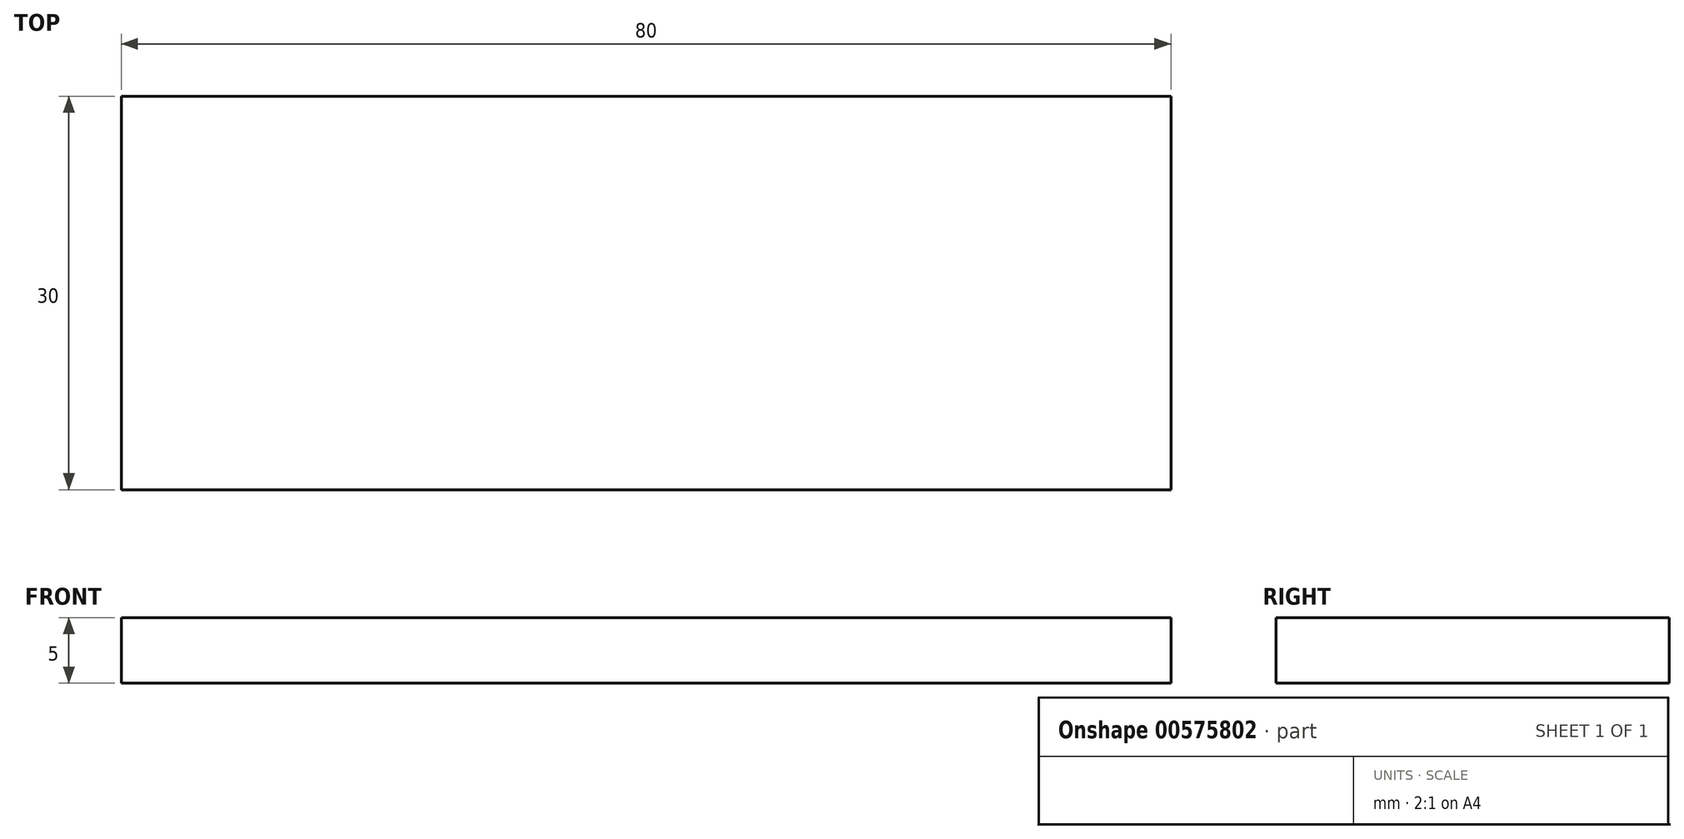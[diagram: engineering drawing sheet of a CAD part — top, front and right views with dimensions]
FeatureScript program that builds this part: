
annotation { "Feature Type Name" : "Feature", "Feature Type Description" : "" }
export const myFeature = defineFeature(function(context is Context, id is Id, definition is map)
    precondition{}
    {
        {
            var Q0;
            Q0=qCreatedBy(makeId("Top.planeOp"),FACE);
            var sketch = newSketch(context, id + "F0", { "sketchPlane" : qUnion([Q0])});
            skLineSegment(sketch, "E0.bottom", {"start": v(40, 15) * mm, "end": v(-40, 15) * mm});
            skLineSegment(sketch, "E0.top", {"start": v(40, -15) * mm, "end": v(-40, -15) * mm});
            skLineSegment(sketch, "E0.left", {"start": v(40, 15) * mm, "end": v(40, -15) * mm});
            skLineSegment(sketch, "E0.right", {"start": v(-40, 15) * mm, "end": v(-40, -15) * mm});
            skPoint(sketch, "E0.middle", {"position": v(0, 0) * mm});
            skSolve(sketch);
        }
        {
            var Q0;
            Q0=makeQuery(id+"F0.imprint","IMPRINT",FACE,{"disambiguationData":[TD([[makeQuery(id+"F0.imprint","IMPRINT",EDGE,{"derivedFrom":sQuery(id+"F0.wireOp",EDGE,"E0.bottom")}),1.0]])]});
            extrude(context, id + "F1", {"entities" : qUnion([Q0]), "depth" : 5 * mm, "offsetDistance" : 25.4 * mm});
        }
    });
